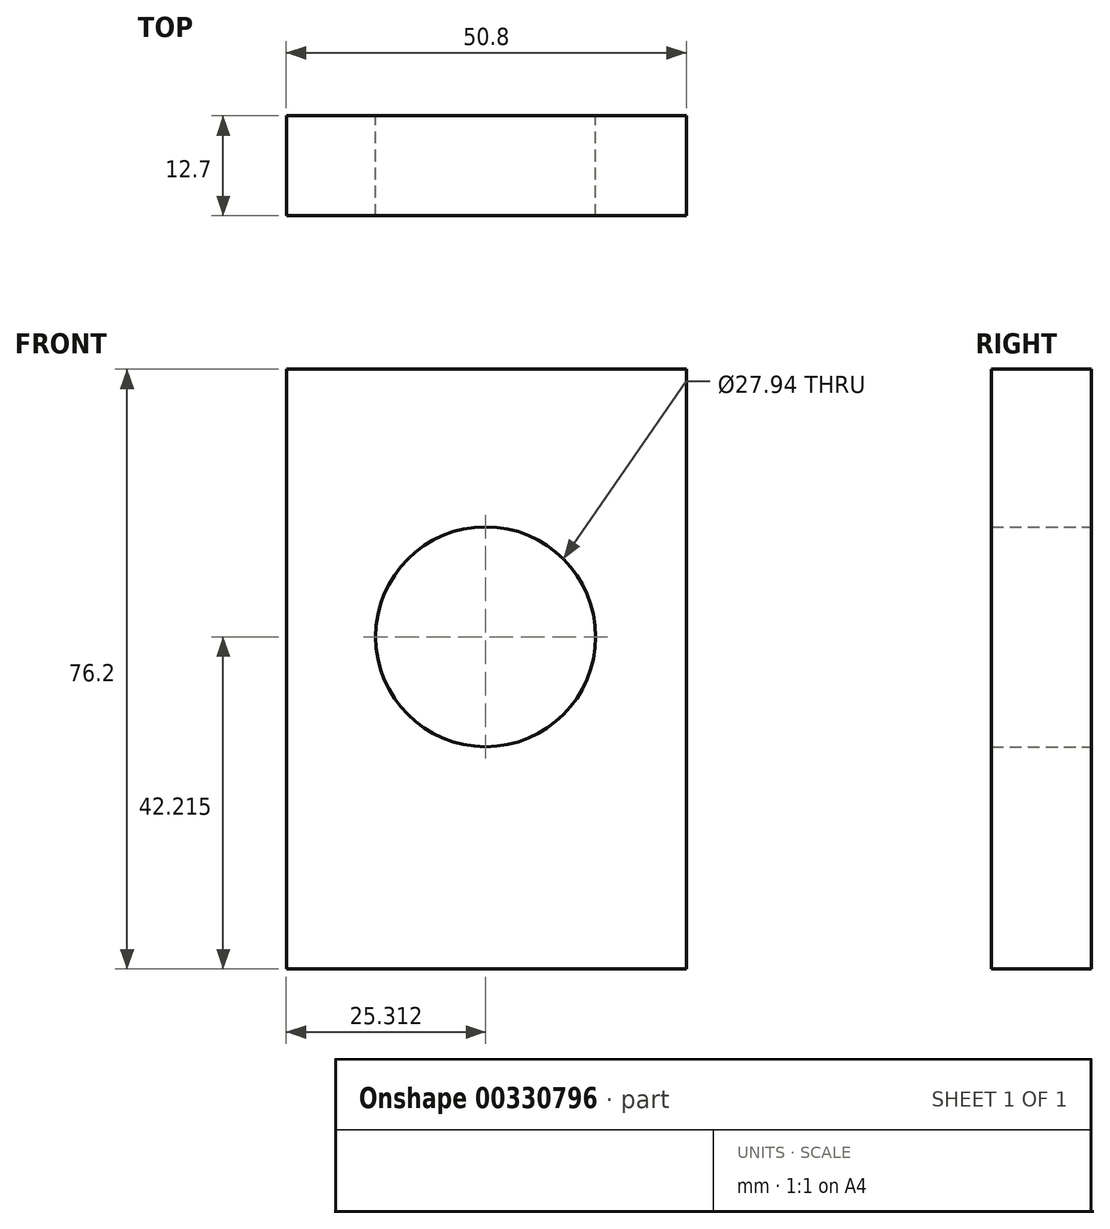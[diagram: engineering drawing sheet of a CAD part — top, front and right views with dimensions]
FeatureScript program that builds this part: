
annotation { "Feature Type Name" : "Feature", "Feature Type Description" : "" }
export const myFeature = defineFeature(function(context is Context, id is Id, definition is map)
    precondition{}
    {
        {
            var Q0;
            Q0=qCreatedBy(makeId("Top.planeOp"),FACE);
            var sketch = newSketch(context, id + "F0", { "sketchPlane" : qUnion([Q0])});
            skLineSegment(sketch, "E0.bottom", {"start": v(-95.45, 35.36) * mm, "end": v(-44.65, 35.36) * mm});
            skLineSegment(sketch, "E0.top", {"start": v(-95.45, 22.66) * mm, "end": v(-44.65, 22.66) * mm});
            skLineSegment(sketch, "E0.left", {"start": v(-95.45, 35.36) * mm, "end": v(-95.45, 22.66) * mm});
            skLineSegment(sketch, "E0.right", {"start": v(-44.65, 35.36) * mm, "end": v(-44.65, 22.66) * mm});
            skSolve(sketch);
        }
        {
            var Q0;
            Q0=makeQuery(id+"F0.imprint","IMPRINT",FACE,{"disambiguationData":[TD([[makeQuery(id+"F0.imprint","IMPRINT",EDGE,{"derivedFrom":sQuery(id+"F0.wireOp",EDGE,"E0.bottom")}),-1.0]])]});
            extrude(context, id + "F1", {"entities" : qUnion([Q0]), "depth" : 76.2 * mm});
        }
        {
            var Q0;
            Q0=makeQuery(id+"F1.opExtrude","SWEPT_FACE",FACE,{"disambiguationData":[OSD([sQuery(id+"F0.wireOp",EDGE,"E0.bottom")])]});
            var sketch = newSketch(context, id + "F2", { "sketchPlane" : qUnion([Q0])});
            skCircle(sketch, "E1", {"center": v(70.14, 42.22) * mm, "radius": 13.97 * mm});
            skSolve(sketch);
        }
        {
            var Q0;
            Q0=makeQuery(id+"F2.imprint","IMPRINT",FACE,{"disambiguationData":[TD([[makeQuery(id+"F2.imprint","IMPRINT",EDGE,{"derivedFrom":sQuery(id+"F2.wireOp",EDGE,"E1")}),1.0]])]});
            extrude(context, id + "F3", {"entities" : qUnion([Q0]), "operationType" : NewBodyOperationType.REMOVE, "oppositeDirection" : true, "depth" : 25.4 * mm});
        }
    });
